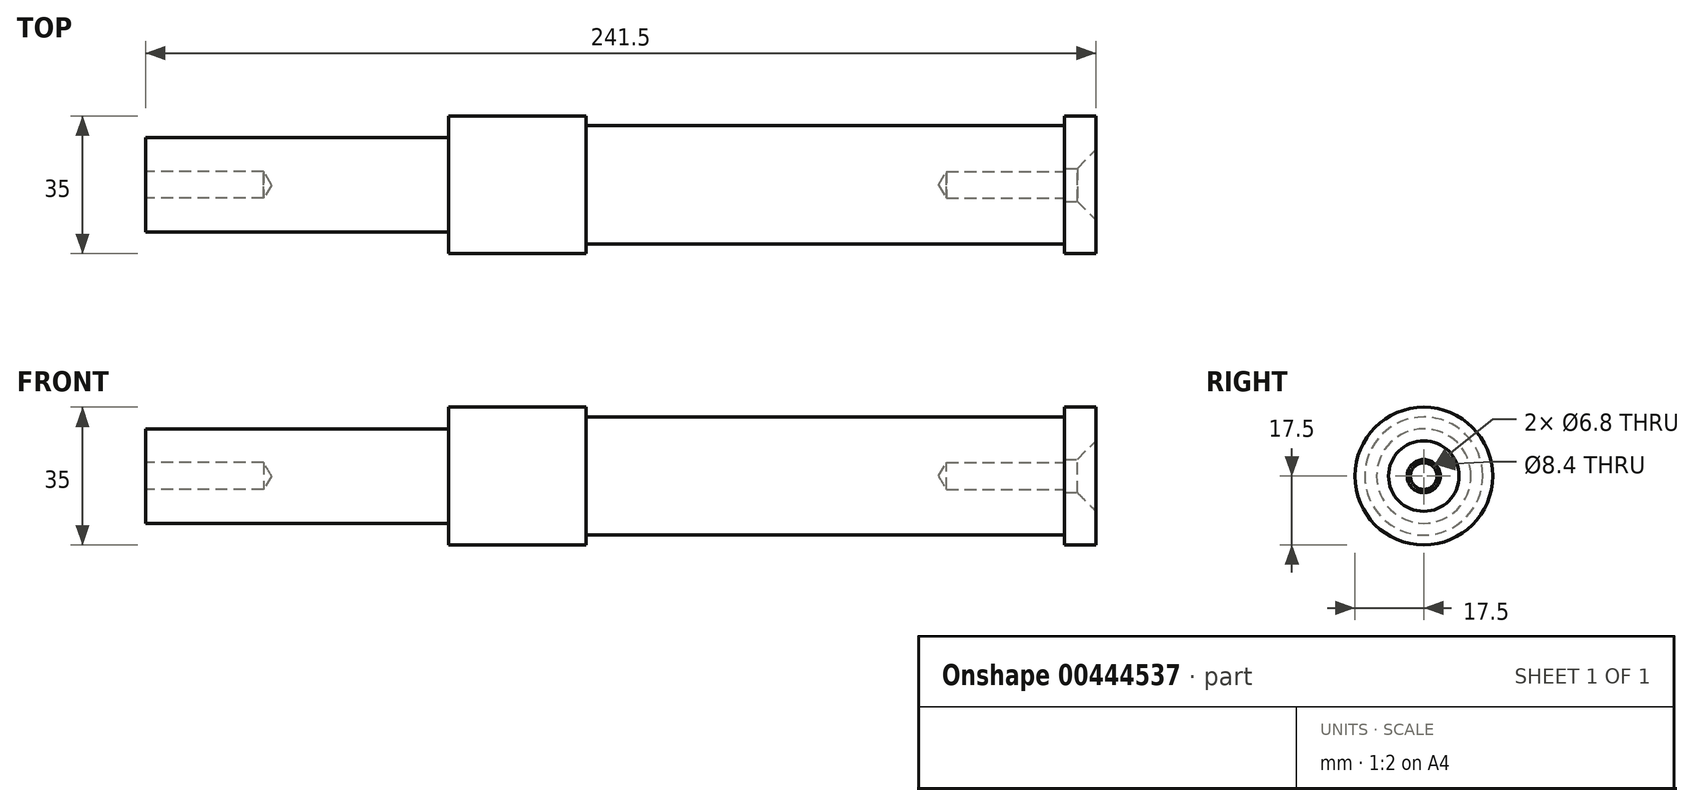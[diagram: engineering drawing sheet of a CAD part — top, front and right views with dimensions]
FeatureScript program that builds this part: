
annotation { "Feature Type Name" : "Feature", "Feature Type Description" : "" }
export const myFeature = defineFeature(function(context is Context, id is Id, definition is map)
    precondition{}
    {
        {
            var Q0;
            Q0=qCreatedBy(makeId("Right.planeOp"),FACE);
            var sketch = newSketch(context, id + "F0", { "sketchPlane" : qUnion([Q0])});
            skCircle(sketch, "E0", {"center": v(0, 0) * mm, "radius": 15 * mm});
            skSolve(sketch);
        }
        {
            var Q0;
            Q0=makeQuery(id+"F0.imprint","IMPRINT",FACE,{"disambiguationData":[TD([[makeQuery(id+"F0.imprint","IMPRINT",EDGE,{"derivedFrom":sQuery(id+"F0.wireOp",EDGE,"E0")}),1.0]])]});
            extrude(context, id + "F1", {"entities" : qUnion([Q0]), "oppositeDirection" : true, "depth" : 156.5 * mm});
        }
        {
            var Q0;
            Q0=makeQuery(id+"F1.opExtrude","CAP_FACE",FACE,{"disambiguationData":[OSD([sQuery(id+"F0.wireOp",EDGE,"E0")])],"isStart":false});
            var sketch = newSketch(context, id + "F2", { "sketchPlane" : qUnion([Q0])});
            skCircle(sketch, "E1", {"center": v(0, 0) * mm, "radius": 12 * mm});
            skSolve(sketch);
        }
        {
            var Q0;
            Q0=makeQuery(id+"F2.imprint","IMPRINT",FACE,{"disambiguationData":[TD([[makeQuery(id+"F2.imprint","IMPRINT",EDGE,{"derivedFrom":sQuery(id+"F2.wireOp",EDGE,"E1")}),1.0]])]});
            extrude(context, id + "F3", {"entities" : qUnion([Q0]), "operationType" : NewBodyOperationType.ADD, "depth" : 77 * mm});
        }
        {
            var Q0;
            Q0=makeQuery(id+"F3.opExtrude","CAP_FACE",FACE,{"disambiguationData":[OSD([sQuery(id+"F2.wireOp",EDGE,"E1")])],"isStart":false});
            var sketch = newSketch(context, id + "F4", { "sketchPlane" : qUnion([Q0])});
            skPoint(sketch, "E2", {"position": v(0, 0) * mm});
            skSolve(sketch);
        }
        {
            var Q0;
            Q0=sQuery(id+"F4.wireOp",VERTEX,"E2");
            var Q1;
            Q1=makeQuery(id+"F1.opExtrude","SWEPT_BODY",BODY,{"disambiguationData":[OSD([sQuery(id+"F0.wireOp",EDGE,"E0")])]});
            hole(context, id + "F5", {"style" : HoleStyle.SIMPLE, "endStyle" : HoleEndStyle.BLIND, "standardTappedOrClearance" : lookupTablePath({ "standard" : "ISO", "engagement" : "75%", "pitch" : "1.25 mm", "size" : "M8", "type" : "Tapped" }), "standardBlindInLast" : lookupTablePath({ "standard" : "ISO", "engagement" : "75%", "pitch" : "1.25 mm", "size" : "M8", "type" : "Tapped" }), "holeDiameter" : 6.8 * mm, "showTappedDepth" : true, "holeDepth" : 30 * mm, "isTappedThrough" : true, "tappedDepth" : 26.25 * mm, "tapClearance" : 3, "locations" : qUnion([Q0]), "scope" : qUnion([Q1]), "majorDiameter" : 8 * mm});
        }
        {
            var Q0;
            Q0=makeQuery(id+"F1.opExtrude","CAP_FACE",FACE,{"disambiguationData":[OSD([sQuery(id+"F0.wireOp",EDGE,"E0")])],"isStart":false});
            var sketch = newSketch(context, id + "F6", { "sketchPlane" : qUnion([Q0])});
            skCircle(sketch, "E3", {"center": v(0, 0) * mm, "radius": 17.5 * mm});
            skCircle(sketch, "E4", {"center": v(0, 0) * mm, "radius": 12 * mm});
            skSolve(sketch);
        }
        {
            var Q0;
            Q0=makeQuery(id+"F6.imprint","IMPRINT",FACE,{"disambiguationData":[TD([[makeQuery(id+"F6.imprint","IMPRINT",EDGE,{"derivedFrom":sQuery(id+"F6.wireOp",EDGE,"E3")}),1.0]])]});
            extrude(context, id + "F7", {"entities" : qUnion([Q0]), "operationType" : NewBodyOperationType.ADD, "oppositeDirection" : true, "depth" : 35 * mm});
        }
        {
            var Q0;
            Q0=sQuery(id+"F0.wireOp",VERTEX,"E0.center");
            var Q1;
            Q1=makeQuery(id+"F1.opExtrude","SWEPT_BODY",BODY,{"disambiguationData":[OSD([sQuery(id+"F0.wireOp",EDGE,"E0")])]});
            hole(context, id + "F8", {"style" : HoleStyle.SIMPLE, "endStyle" : HoleEndStyle.BLIND, "standardTappedOrClearance" : lookupTablePath({ "standard" : "ISO", "engagement" : "75%", "pitch" : "1.25 mm", "size" : "M8", "type" : "Tapped" }), "standardBlindInLast" : lookupTablePath({ "standard" : "ISO", "engagement" : "75%", "pitch" : "1.25 mm", "size" : "M8", "type" : "Tapped" }), "holeDiameter" : 6.8 * mm, "showTappedDepth" : true, "holeDepth" : 30 * mm, "isTappedThrough" : true, "tappedDepth" : 26.25 * mm, "tapClearance" : 3, "locations" : qUnion([Q0]), "scope" : qUnion([Q1]), "majorDiameter" : 8 * mm});
        }
        {
            var Q0;
            Q0=qCreatedBy(makeId("Right.planeOp"),FACE);
            var sketch = newSketch(context, id + "F9", { "sketchPlane" : qUnion([Q0])});
            skCircle(sketch, "E5", {"center": v(0, 0) * mm, "radius": 17.5 * mm});
            skSolve(sketch);
        }
        {
            var Q0;
            Q0=makeQuery(id+"F9.imprint","IMPRINT",FACE,{"disambiguationData":[TD([[makeQuery(id+"F9.imprint","IMPRINT",EDGE,{"derivedFrom":sQuery(id+"F9.wireOp",EDGE,"E5")}),1.0]])]});
            extrude(context, id + "F10", {"entities" : qUnion([Q0]), "depth" : 8 * mm});
        }
        {
            var Q0;
            Q0=makeQuery(id+"F10.opExtrude","CAP_FACE",FACE,{"disambiguationData":[OSD([sQuery(id+"F9.wireOp",EDGE,"E5")])],"isStart":false});
            var sketch = newSketch(context, id + "F11", { "sketchPlane" : qUnion([Q0])});
            skPoint(sketch, "E6", {"position": v(0, 0) * mm});
            skSolve(sketch);
        }
        {
            var Q0;
            Q0=sQuery(id+"F11.wireOp",VERTEX,"E6");
            var Q1;
            Q1=makeQuery(id+"F10.opExtrude","SWEPT_BODY",BODY,{"disambiguationData":[OSD([sQuery(id+"F9.wireOp",EDGE,"E5")])]});
            hole(context, id + "F12", {"style" : HoleStyle.C_SINK, "endStyle" : HoleEndStyle.BLIND, "standardTappedOrClearance" : lookupTablePath({ "standard" : "ISO", "fit" : "Close", "size" : "M8", "type" : "Clearance" }), "standardBlindInLast" : lookupTablePath({ "fit" : "Close", "standard" : "ISO", "size" : "M8", "type" : "Clearance" }), "holeDiameter" : 8.4 * mm, "cSinkDiameter" : 17.92 * mm, "cSinkAngle" : 90 * degree, "holeDepth" : 30 * mm, "isTappedThrough" : true, "tappedDepth" : 26.25 * mm, "tapClearance" : 3, "locations" : qUnion([Q0]), "scope" : qUnion([Q1])});
        }
    });
